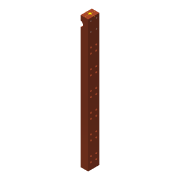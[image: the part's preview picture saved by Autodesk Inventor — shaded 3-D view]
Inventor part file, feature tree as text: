
AUTODESK INVENTOR PART (.ipt)
format: ipt  version: 2016 SP2 (Build 200236200, 236)  size: 131,584 bytes
history: native  units: mm
features: other x3, sketch x2, hole x2
ambient origin geometry x8: Origin, YZ Plane, XZ Plane, XY Plane, X Axis, Y Axis, Z Axis, Center Point
bodies: Solid1 (feature_tree)
feature tree (7):
  other  "17-0028-0025.ipt"
  sketch  "Sketch1"  dims[d0=10.0mm]
  hole  "Hole3"  [1 undecoded]
  other  "Solid3::17-0028-0025.ipt"
  other  "TaggingFeature1"
  sketch  "Sketch3"  dims[d8=4.134mm d9=22.570758mm d10=4.0mm d11=2.0mm d12=90.0deg d13=25.070758mm d14=120.0deg]
  hole  "Hole2"  [1 undecoded]
note: 2 required parameter values undecoded (feature->parameter linkage not recoverable at this tier; creation-order binding heuristic only, values carry confidence <= 0.55)
